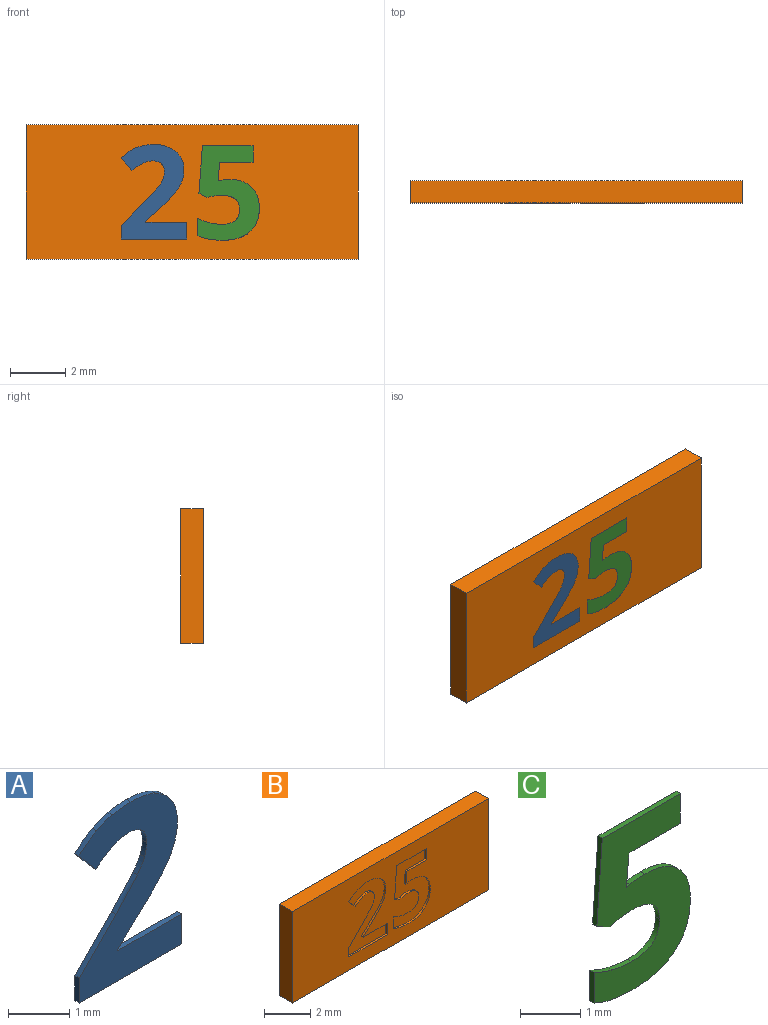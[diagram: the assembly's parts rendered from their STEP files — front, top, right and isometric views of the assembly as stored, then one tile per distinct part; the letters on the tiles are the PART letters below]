
ASSEMBLY  parts=3 mates=2
PART A: 26 faces, bbox 2.4x0.1x3.4 mm
  f0: plane 3.42x2.37mm, normal (0,-1,0), area 4.2mm2, adj f1,f2,f3,f4,f5,f6,f7,f8
  f1: plane 1.47x0.1mm, normal (0,0,1), area 0.1mm2, adj f0,f2,f22,f24
  f2: plane 0.1x0.03mm, normal (1,0,0), area 0mm2, adj f0,f1,f3,f22
  f3: plane 0.43x0.41mm, normal (0.69,0,-0.73), area 0.1mm2, adj f0,f2,f4,f22
  f4: extruded ~0.61x0.61mm, area 0.1mm2, adj f0,f3,f5,f22
  f5: extruded ~0.42x0.25mm, area 0mm2, adj f0,f4,f6,f22
  f6: extruded ~0.44x0.1mm, area 0mm2, adj f0,f5,f7,f22
  f7: extruded ~0.48x0.13mm, area 0.1mm2, adj f0,f6,f8,f22
  f8: extruded ~0.38x0.32mm, area 0.1mm2, adj f0,f7,f9,f22
  f9: extruded ~0.56x0.12mm, area 0.1mm2, adj f0,f8,f10,f22
  f10: extruded ~0.43x0.1mm, area 0mm2, adj f0,f9,f11,f22
  f11: extruded ~0.36x0.13mm, area 0mm2, adj f0,f10,f12,f22
  f12: extruded ~0.41x0.3mm, area 0.1mm2, adj f0,f11,f13,f22
  f13: plane 0.46x0.39mm, normal (-0.76,0,-0.65), area 0.1mm2, adj f0,f12,f14,f22
  f14: extruded ~0.39x0.26mm, area 0mm2, adj f0,f13,f15,f22
  f15: extruded ~0.38x0.1mm, area 0mm2, adj f0,f14,f16,f22
  f16: extruded ~0.3x0.1mm, area 0mm2, adj f0,f15,f17,f22
  f17: extruded ~0.3x0.11mm, area 0mm2, adj f0,f16,f18,f22
  f18: extruded ~0.26x0.1mm, area 0mm2, adj f0,f17,f19,f22
  f19: extruded ~0.28x0.17mm, area 0mm2, adj f0,f18,f20,f22
  f20: extruded ~0.53x0.49mm, area 0.1mm2, adj f0,f19,f21,f22
  f21: plane 0.86x0.85mm, normal (-0.71,0,0.7), area 0.1mm2, adj f0,f20,f22,f23
  f22: plane 3.42x2.37mm, normal (0,1,0), area 4.2mm2, adj f1,f2,f3,f4,f5,f6,f7,f8
  f23: plane 0.5x0.1mm, normal (-1,0,0), area 0mm2, adj f0,f21,f22,f25
  f24: plane 0.6x0.1mm, normal (1,0,0), area 0.1mm2, adj f0,f1,f22,f25
  f25: plane 2.36x0.1mm, normal (0,0,-1), area 0.2mm2, adj f0,f22,f23,f24
PART B: 52 faces, bbox 12x0.8x4.9 mm
  f0: plane 12x4.85mm, normal (0,-1,0), area 49.5mm2, adj f1,f2,f3,f4,f6,f7,f8,f9
  f1: plane 12x0.8mm, normal (0,0,-1), area 9.6mm2, adj f0,f2,f4,f5
  f2: plane 4.85x0.8mm, normal (1,0,0), area 3.9mm2, adj f0,f1,f3,f5
  f3: plane 12x0.8mm, normal (0,0,1), area 9.6mm2, adj f0,f2,f4,f5
  f4: plane 4.85x0.8mm, normal (-1,0,0), area 3.9mm2, adj f0,f1,f3,f5
  f5: plane 12x4.85mm, normal (0,1,0), area 58.2mm2, adj f1,f2,f3,f4
  f6: extruded ~0.35x0.1mm, area 0mm2, adj f0,f7,f25,f26
  f7: plane 0.1x0.08mm, normal (0.2,0,-0.98), area 0mm2, adj f0,f6,f8,f26
  f8: plane 0.66x0.1mm, normal (-1,0,0.09), area 0.1mm2, adj f0,f7,f9,f26
  f9: plane 1.2x0.1mm, normal (0,0,1), area 0.1mm2, adj f0,f8,f10,f26
  f10: plane 0.6x0.1mm, normal (-1,0,0), area 0.1mm2, adj f0,f9,f11,f26
  f11: plane 1.83x0.1mm, normal (0,0,-1), area 0.2mm2, adj f0,f10,f12,f26
  f12: plane 1.72x0.13mm, normal (1,0,-0.07), area 0.2mm2, adj f0,f11,f13,f26
  f13: plane 0.28x0.15mm, normal (0.47,0,0.88), area 0mm2, adj f0,f12,f14,f26
  f14: extruded ~0.24x0.1mm, area 0mm2, adj f0,f13,f15,f26
  f15: extruded ~0.27x0.1mm, area 0mm2, adj f0,f14,f16,f26
  f16: extruded ~0.68x0.51mm, area 0.1mm2, adj f0,f15,f17,f26
  f17: extruded ~0.65x0.54mm, area 0.1mm2, adj f0,f16,f18,f26
  f18: extruded ~0.46x0.1mm, area 0mm2, adj f0,f17,f19,f26
  f19: extruded ~0.42x0.16mm, area 0mm2, adj f0,f18,f20,f26
  f20: plane 0.62x0.1mm, normal (1,0,0), area 0.1mm2, adj f0,f19,f21,f26
  f21: extruded ~0.91x0.18mm, area 0.1mm2, adj f0,f20,f22,f26
  f22: extruded ~1x0.3mm, area 0.1mm2, adj f0,f21,f23,f26
  f23: extruded ~0.87x0.35mm, area 0.1mm2, adj f0,f22,f24,f26
  f24: extruded ~0.75x0.29mm, area 0.1mm2, adj f0,f23,f25,f26
  f25: extruded ~0.78x0.27mm, area 0.1mm2, adj f0,f6,f24,f26
  f26: plane 3.42x2.25mm, normal (0,-1,0), area 4.5mm2, adj f6,f7,f8,f9,f10,f11,f12,f13
  f27: plane 0.6x0.1mm, normal (-1,0,0), area 0.1mm2, adj f0,f28,f50,f51
  f28: plane 1.47x0.1mm, normal (0,0,-1), area 0.1mm2, adj f0,f27,f29,f51
  f29: plane 0.1x0.03mm, normal (-1,0,0), area 0mm2, adj f0,f28,f30,f51
  f30: plane 0.43x0.41mm, normal (-0.69,0,0.73), area 0.1mm2, adj f0,f29,f31,f51
  f31: extruded ~0.61x0.61mm, area 0.1mm2, adj f0,f30,f32,f51
  f32: extruded ~0.42x0.25mm, area 0mm2, adj f0,f31,f33,f51
  f33: extruded ~0.44x0.1mm, area 0mm2, adj f0,f32,f34,f51
  f34: extruded ~0.48x0.13mm, area 0.1mm2, adj f0,f33,f35,f51
  f35: extruded ~0.38x0.32mm, area 0.1mm2, adj f0,f34,f36,f51
  f36: extruded ~0.56x0.12mm, area 0.1mm2, adj f0,f35,f37,f51
  f37: extruded ~0.43x0.1mm, area 0mm2, adj f0,f36,f38,f51
  f38: extruded ~0.36x0.13mm, area 0mm2, adj f0,f37,f39,f51
  f39: extruded ~0.41x0.3mm, area 0.1mm2, adj f0,f38,f40,f51
  f40: plane 0.46x0.39mm, normal (0.76,0,0.65), area 0.1mm2, adj f0,f39,f41,f51
  f41: extruded ~0.39x0.26mm, area 0mm2, adj f0,f40,f42,f51
  f42: extruded ~0.38x0.1mm, area 0mm2, adj f0,f41,f43,f51
  f43: extruded ~0.3x0.1mm, area 0mm2, adj f0,f42,f44,f51
  f44: extruded ~0.3x0.11mm, area 0mm2, adj f0,f43,f45,f51
  f45: extruded ~0.26x0.1mm, area 0mm2, adj f0,f44,f46,f51
  f46: extruded ~0.28x0.17mm, area 0mm2, adj f0,f45,f47,f51
  f47: extruded ~0.53x0.49mm, area 0.1mm2, adj f0,f46,f48,f51
  f48: plane 0.86x0.85mm, normal (0.71,0,-0.7), area 0.1mm2, adj f0,f47,f49,f51
  f49: plane 0.5x0.1mm, normal (1,0,0), area 0mm2, adj f0,f48,f50,f51
  f50: plane 2.36x0.1mm, normal (0,0,1), area 0.2mm2, adj f0,f27,f49,f51
  f51: plane 3.42x2.37mm, normal (0,-1,0), area 4.2mm2, adj f27,f28,f29,f30,f31,f32,f33,f34
PART C: 22 faces, bbox 2.3x0.1x3.4 mm
  f0: plane 3.42x2.25mm, normal (0,-1,0), area 4.5mm2, adj f1,f2,f3,f4,f5,f6,f7,f8
  f1: plane 0.1x0.08mm, normal (-0.2,0,0.98), area 0mm2, adj f0,f2,f18,f20
  f2: plane 0.66x0.1mm, normal (1,0,-0.09), area 0.1mm2, adj f0,f1,f3,f18
  f3: plane 1.2x0.1mm, normal (0,0,-1), area 0.1mm2, adj f0,f2,f4,f18
  f4: plane 0.6x0.1mm, normal (1,0,0), area 0.1mm2, adj f0,f3,f5,f18
  f5: plane 1.83x0.1mm, normal (0,0,1), area 0.2mm2, adj f0,f4,f6,f18
  f6: plane 1.72x0.13mm, normal (-1,0,0.07), area 0.2mm2, adj f0,f5,f7,f18
  f7: plane 0.28x0.15mm, normal (-0.47,0,-0.88), area 0mm2, adj f0,f6,f8,f18
  f8: extruded ~0.24x0.1mm, area 0mm2, adj f0,f7,f9,f18
  f9: extruded ~0.27x0.1mm, area 0mm2, adj f0,f8,f10,f18
  f10: extruded ~0.68x0.51mm, area 0.1mm2, adj f0,f9,f11,f18
  f11: extruded ~0.65x0.54mm, area 0.1mm2, adj f0,f10,f12,f18
  f12: extruded ~0.46x0.1mm, area 0mm2, adj f0,f11,f13,f18
  f13: extruded ~0.42x0.16mm, area 0mm2, adj f0,f12,f14,f18
  f14: plane 0.62x0.1mm, normal (-1,0,0), area 0.1mm2, adj f0,f13,f15,f18
  f15: extruded ~0.91x0.18mm, area 0.1mm2, adj f0,f14,f16,f18
  f16: extruded ~1x0.3mm, area 0.1mm2, adj f0,f15,f17,f18
  f17: extruded ~0.87x0.35mm, area 0.1mm2, adj f0,f16,f18,f19
  f18: plane 3.42x2.25mm, normal (0,1,0), area 4.5mm2, adj f1,f2,f3,f4,f5,f6,f7,f8
  f19: extruded ~0.75x0.29mm, area 0.1mm2, adj f0,f17,f18,f21
  f20: extruded ~0.35x0.1mm, area 0mm2, adj f0,f1,f18,f21
  f21: extruded ~0.78x0.27mm, area 0.1mm2, adj f0,f18,f19,f20
PLACE A t=(-2.91,0.4,0.02)mm
PLACE B t=(-0.02,0.4,0.02)mm
PLACE C t=(-0.24,0.4,0.02)mm
MATE fastened A.f0 <-> B.f0  axis (0,-1,0) through (-2.57,-0.4,-1.68)mm
MATE fastened C.f0 <-> B.f0  axis (0,-1,0) through (0.16,-0.4,-1.54)mm
